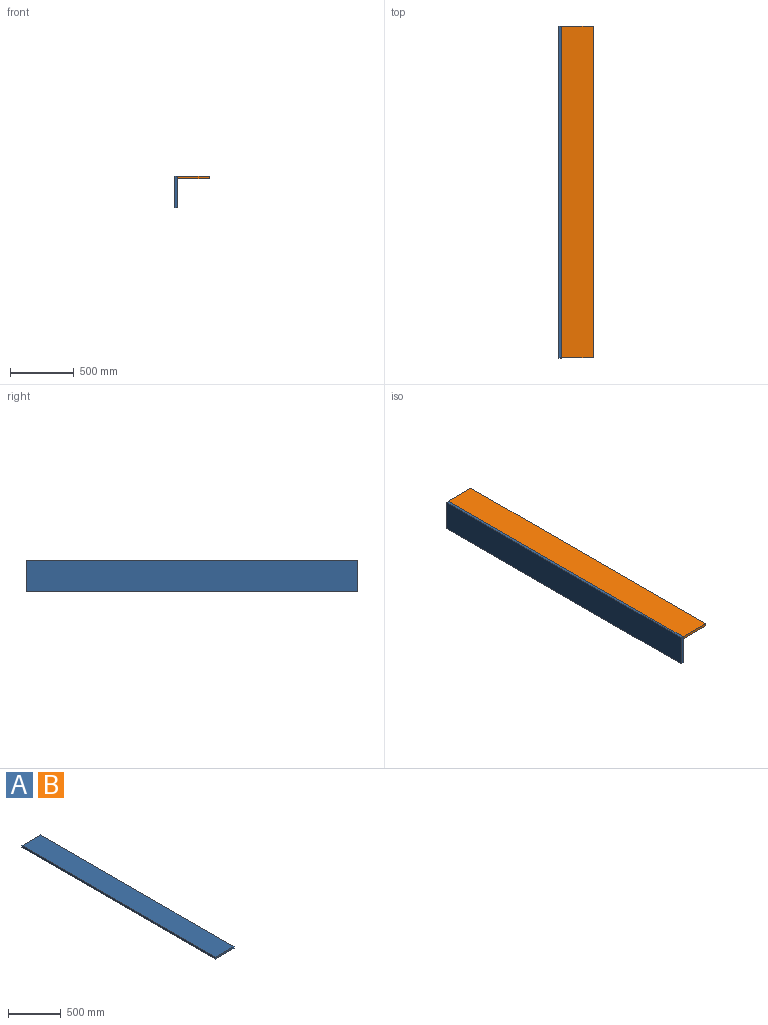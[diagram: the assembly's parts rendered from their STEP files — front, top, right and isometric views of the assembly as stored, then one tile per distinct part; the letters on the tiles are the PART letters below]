
ASSEMBLY  parts=2 mates=1
PART A: 6 faces, bbox 250x2600x21 mm
  f0: plane 2600x250mm, normal (0,0,1), area 650000mm2, adj f1,f3,f4,f5
  f1: plane 2600x21mm, normal (-1,0,0), area 54600mm2, adj f0,f2,f4,f5
  f2: plane 2600x250mm, normal (0,0,-1), area 650000mm2, adj f1,f3,f4,f5
  f3: plane 2600x21mm, normal (1,0,0), area 54600mm2, adj f0,f2,f4,f5
  f4: plane 250x21mm, normal (0,-1,0), area 5250mm2, adj f0,f1,f2,f3
  f5: plane 250x21mm, normal (0,1,0), area 5250mm2, adj f0,f1,f2,f3
PART B: same geometry as A
PLACE A rot(axis=(0,-1,0),90deg) t=(-384.33,766.19,-833.82)mm
PLACE B t=(-363.33,766.19,-583.82)mm
MATE fastened A.f4 <-> B.f4  axis (0,-1,0) through (-363.33,-1833.81,-583.82)mm
